# Revit family: P6059-20
name_source: partatom
category: Lighting Fixtures
revit_build: Autodesk Revit 2014 (Build: 20130308_1515(x64)
units: mm (PartAtom-declared; Revit-internal decimal feet)

## types (1)
- P6059-20
    Apparent Load = 100 VA
    Color Filter = 16777215
    Connector Description = Lighting Connector
    Default Elevation = 72 "
    Description = Essential Collection One-Light Small Wall Lantern
    Dimming Lamp Color Temperature Shift = <None>
    Features = Antique Bronze finish.
Etched umber linen glass.
Powdercoat finish.
    Fixture distribution = Direct
    Glass = Paint - Hubbell - White Texture
    Gold = Hubbell - Gold
    Height = 6.5 "
    Housing Material = Wood Planks
    Lamp = LED
    Load Classification = Lighting
    Manufacturer = Progress Lighting
    Model = P6059-20
    Photometric Web File = generic
    Power Factor = 1
    Product Documentation Link = https://hubbellcdn.com
    Product Link = https://www.hubbell.com
    Support = Paint - Hubbell - Light Silver
    Tilt Angle = 60.00°
    URL = https://www.hubbell.com
    Voltage = 120 V
    Warranty = 1 year Warranty
    Wattage Comments = 100W
    Watts = 100 W
    Width = 4.5 "

## geometry (parser evidence)
native form markers: Sweep x3
no freeform markers — native parametric forms only
